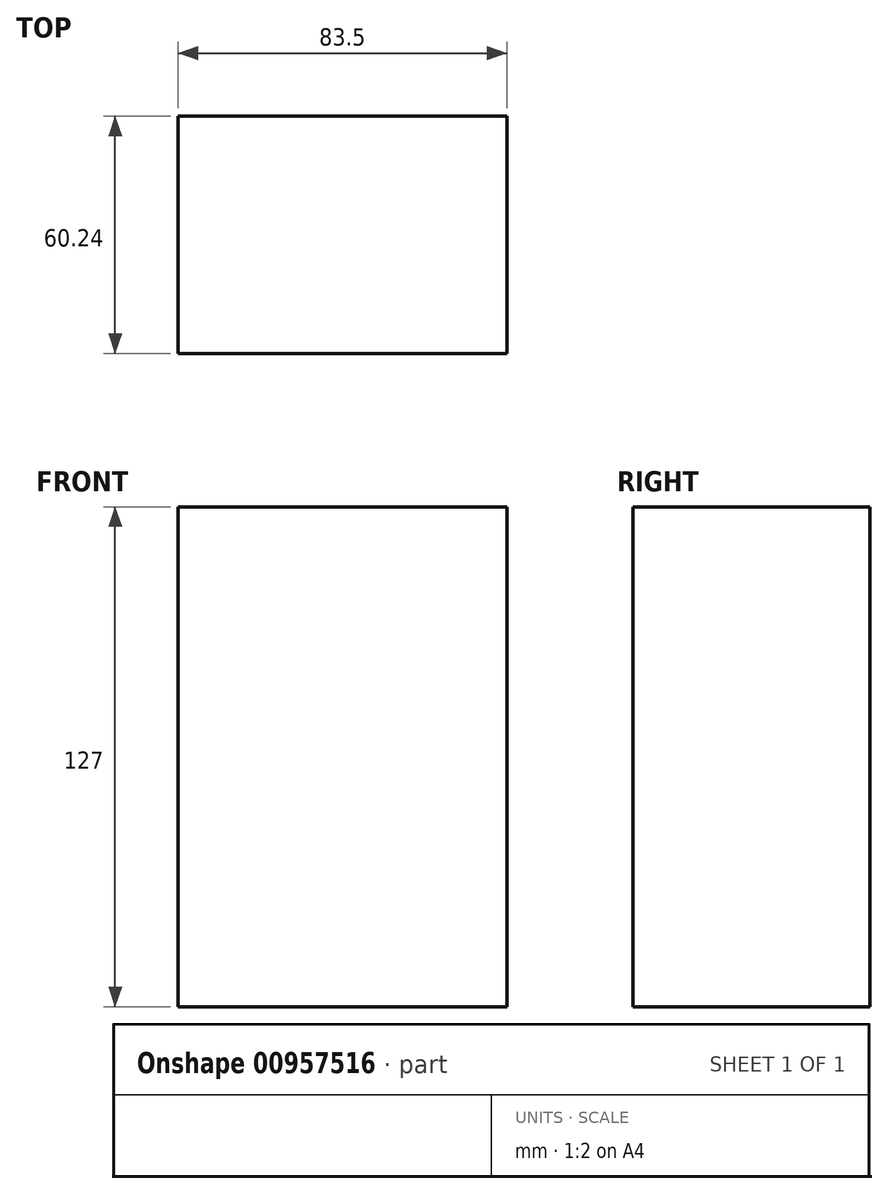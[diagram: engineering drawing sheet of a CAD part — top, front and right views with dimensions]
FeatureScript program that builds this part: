
annotation { "Feature Type Name" : "Feature", "Feature Type Description" : "" }
export const myFeature = defineFeature(function(context is Context, id is Id, definition is map)
    precondition{}
    {
        {
            var Q0;
            Q0=qCreatedBy(makeId("Top.planeOp"),FACE);
            var sketch = newSketch(context, id + "F0", { "sketchPlane" : qUnion([Q0])});
            skLineSegment(sketch, "E0.bottom", {"start": v(-41.75, 30.12) * mm, "end": v(41.75, 30.12) * mm});
            skLineSegment(sketch, "E0.top", {"start": v(-41.75, -30.12) * mm, "end": v(41.75, -30.12) * mm});
            skLineSegment(sketch, "E0.left", {"start": v(-41.75, 30.12) * mm, "end": v(-41.75, -30.12) * mm});
            skLineSegment(sketch, "E0.right", {"start": v(41.75, 30.12) * mm, "end": v(41.75, -30.12) * mm});
            skPoint(sketch, "E0.middle", {"position": v(0, 0) * mm});
            skSolve(sketch);
        }
        {
            var Q0;
            Q0=makeQuery(id+"F0.imprint","IMPRINT",FACE,{"disambiguationData":[TD([[makeQuery(id+"F0.imprint","IMPRINT",EDGE,{"derivedFrom":sQuery(id+"F0.wireOp",EDGE,"E0.bottom")}),-1.0]])]});
            extrude(context, id + "F1", {"entities" : qUnion([Q0]), "endBound" : BoundingType.SYMMETRIC, "depth" : 127 * mm, "offsetDistance" : 25.4 * mm});
        }
    });
